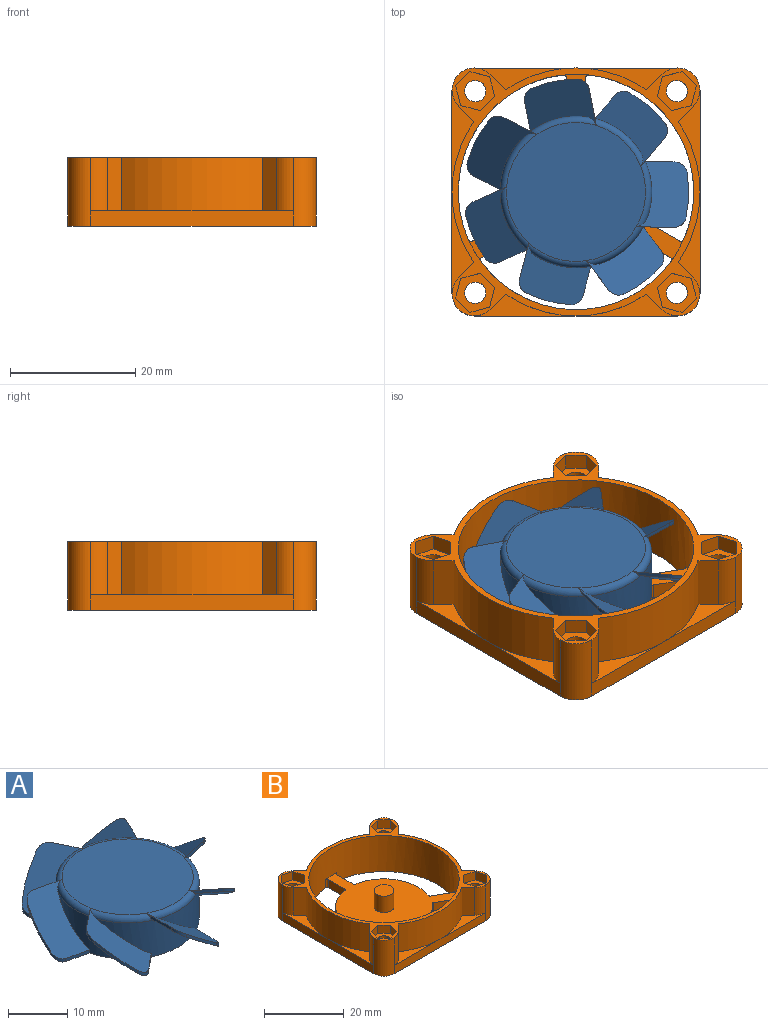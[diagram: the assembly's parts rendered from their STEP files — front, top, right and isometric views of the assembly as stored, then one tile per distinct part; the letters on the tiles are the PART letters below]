
ASSEMBLY  parts=2 mates=1
PART A: 67 faces, bbox 36.1x35.6x8.6 mm
  f0: torus R=11.1mm, axis (0,0,1), area 15.8mm2, adj f22,f25,f27,f37,f41
  f1: torus R=11.1mm, axis (0,0,1), area 15.8mm2, adj f18,f21,f23,f37,f40
  f2: torus R=11.1mm, axis (0,0,1), area 15.8mm2, adj f14,f17,f19,f37,f39
  f3: torus R=11.1mm, axis (0,0,1), area 15.8mm2, adj f10,f13,f15,f37,f38
  f4: torus R=11.1mm, axis (0,0,1), area 15.8mm2, adj f6,f9,f11,f34,f37
  f5: torus R=11.1mm, axis (0,0,1), area 15.8mm2, adj f7,f30,f33,f35,f37
  f6: plane 11.46x8.73mm, normal (0.13,0.58,-0.8), area 78mm2, adj f4,f8,f9,f34,f49,f52,f53
  f7: plane 11.36x9.65mm, normal (-0.13,-0.58,0.8), area 78.4mm2, adj f5,f8,f9,f35,f49,f52,f53
  f8: plane 4.65x1.06mm, normal (-0.22,-0.97,0), area 3mm2, adj f6,f7,f35,f52
  f9: plane 5.85x1.42mm, normal (0.22,0.97,0), area 3.2mm2, adj f4,f6,f7,f53
  f10: plane 5.41x2.67mm, normal (0.9,0.43,0), area 3.2mm2, adj f3,f11,f13,f54
  f11: plane 12.23x10mm, normal (-0.54,-0.26,0.8), area 78.4mm2, adj f4,f10,f12,f34,f48,f54,f55
  f12: plane 4.29x2.07mm, normal (-0.9,-0.43,0), area 3mm2, adj f11,f13,f34,f55
  f13: plane 11.88x10.1mm, normal (0.54,0.26,-0.8), area 78mm2, adj f3,f10,f12,f38,f48,f54,f55
  f14: plane 5.41x2.67mm, normal (0.9,-0.43,0), area 3.2mm2, adj f2,f15,f17,f56
  f15: plane 11.74x11.01mm, normal (-0.54,0.26,0.8), area 78.4mm2, adj f3,f14,f16,f38,f47,f56,f57
  f16: plane 4.29x2.07mm, normal (-0.9,0.43,0), area 3mm2, adj f15,f17,f38,f57
  f17: plane 11.84x10.17mm, normal (0.54,-0.26,-0.8), area 78mm2, adj f2,f14,f16,f39,f47,f56,f57
  f18: plane 5.85x1.42mm, normal (0.22,-0.97,0), area 3.2mm2, adj f1,f19,f21,f58
  f19: plane 11.61x8.55mm, normal (-0.13,0.58,0.8), area 78.4mm2, adj f2,f18,f20,f39,f46,f58,f59
  f20: plane 4.65x1.06mm, normal (-0.22,0.97,0), area 3mm2, adj f19,f21,f39,f59
  f21: plane 11.48x8.65mm, normal (0.13,-0.58,-0.8), area 78mm2, adj f1,f18,f20,f40,f46,f58,f59
  f22: plane 4.71x3.78mm, normal (-0.62,-0.78,0), area 3.2mm2, adj f0,f23,f25,f60
  f23: plane 11.92x11.63mm, normal (0.37,0.47,0.8), area 78.4mm2, adj f1,f22,f24,f40,f45,f60,f61
  f24: plane 3.73x2.97mm, normal (0.62,0.78,0), area 3mm2, adj f23,f25,f40,f61
  f25: plane 11.73x11.2mm, normal (-0.37,-0.47,-0.8), area 78mm2, adj f0,f22,f24,f41,f45,f60,f61
  f26: plane 6x0.74mm, normal (-1,0,0), area 3.2mm2, adj f27,f29,f62,f66
  f27: plane 10.51x8.23mm, normal (0.6,0,0.8), area 78.4mm2, adj f0,f26,f28,f41,f44,f62,f63
  f28: plane 4.76x0.63mm, normal (1,0,0), area 3mm2, adj f27,f29,f41,f63
  f29: plane 10.61x7.99mm, normal (-0.6,0,-0.8), area 78mm2, adj f26,f28,f42,f44,f62,f63,f66
  f30: plane 4.71x3.78mm, normal (-0.62,0.78,0), area 3.2mm2, adj f5,f31,f33,f64
  f31: plane 12.33x11.04mm, normal (0.37,-0.47,0.8), area 78.4mm2, adj f30,f32,f42,f43,f64,f65,f66
  f32: plane 3.73x2.97mm, normal (0.62,-0.78,0), area 3mm2, adj f31,f33,f42,f65
  f33: plane 11.78x11.14mm, normal (-0.37,0.47,-0.8), area 78mm2, adj f5,f30,f32,f35,f43,f64,f65
  f34: cylinder r=12.1mm len=14.71mm, axis (0,0,-1), area 75.4mm2, adj f4,f6,f11,f12,f36
  f35: cylinder r=12.1mm len=17.27mm, axis (0,0,-1), area 75.4mm2, adj f5,f7,f8,f33,f36
  f36: plane 24.2x24.2mm, normal (0,0,-1), area 440.3mm2, adj f34,f35,f38,f39,f40,f41,f42,f50
  f37: plane 22.2x22.2mm, normal (0,0,1), area 387.1mm2, adj f0,f1,f2,f3,f4,f5,f66
  f38: cylinder r=12.1mm len=17.96mm, axis (0,0,-1), area 75.4mm2, adj f3,f13,f15,f16,f36
  f39: cylinder r=12.1mm len=13.37mm, axis (0,0,-1), area 75.4mm2, adj f2,f17,f19,f20,f36
  f40: cylinder r=12.1mm len=17.74mm, axis (0,0,-1), area 75.4mm2, adj f1,f21,f23,f24,f36
  f41: cylinder r=12.1mm len=15.71mm, axis (0,0,-1), area 75.4mm2, adj f0,f25,f27,f28,f36
  f42: cylinder r=12.1mm len=16.64mm, axis (0,0,-1), area 75.4mm2, adj f29,f31,f32,f36,f66
  f43: cylinder r=18mm len=6.11mm, axis (0,0,1), area 4.6mm2, adj f31,f33,f64,f65
  f44: cylinder r=18mm len=7.31mm, axis (0,0,1), area 4.6mm2, adj f27,f29,f62,f63
  f45: cylinder r=18mm len=6.11mm, axis (0,0,1), area 4.6mm2, adj f23,f25,f60,f61
  f46: cylinder r=18mm len=7.13mm, axis (0,0,1), area 4.6mm2, adj f19,f21,f58,f59
  f47: cylinder r=18mm len=6.59mm, axis (0,0,1), area 4.6mm2, adj f15,f17,f56,f57
  f48: cylinder r=18mm len=6.59mm, axis (0,0,1), area 4.6mm2, adj f11,f13,f54,f55
  f49: cylinder r=18mm len=7.13mm, axis (0,0,1), area 4.6mm2, adj f6,f7,f52,f53
  f50: cylinder r=2.5mm len=5mm, axis (0,0,-1), area 78.5mm2, adj f36,f51
  f51: plane 5x5mm, normal (0,0,-1), area 19.6mm2, adj f50
  f52: cylinder r=2mm len=1.99mm, axis (0,0,1), area 1.7mm2, adj f6,f7,f8,f49
  f53: cylinder r=2mm len=2.26mm, axis (0,0,1), area 1.7mm2, adj f6,f7,f9,f49
  f54: cylinder r=2mm len=2.29mm, axis (0,0,1), area 1.7mm2, adj f10,f11,f13,f48
  f55: cylinder r=2mm len=2.46mm, axis (0,0,1), area 1.7mm2, adj f11,f12,f13,f48
  f56: cylinder r=2mm len=2.46mm, axis (0,0,1), area 1.7mm2, adj f14,f15,f17,f47
  f57: cylinder r=2mm len=2.29mm, axis (0,0,1), area 1.7mm2, adj f15,f16,f17,f47
  f58: cylinder r=2mm len=1.99mm, axis (0,0,1), area 1.7mm2, adj f18,f19,f21,f46
  f59: cylinder r=2mm len=2.26mm, axis (0,0,1), area 1.7mm2, adj f19,f20,f21,f46
  f60: cylinder r=2mm len=2.52mm, axis (0,0,1), area 1.7mm2, adj f22,f23,f25,f45
  f61: cylinder r=2mm len=2.47mm, axis (0,0,1), area 1.7mm2, adj f23,f24,f25,f45
  f62: cylinder r=2mm len=1.96mm, axis (0,0,1), area 1.7mm2, adj f26,f27,f29,f44
  f63: cylinder r=2mm len=1.96mm, axis (0,0,1), area 1.7mm2, adj f27,f28,f29,f44
  f64: cylinder r=2mm len=2.47mm, axis (0,0,1), area 1.7mm2, adj f30,f31,f33,f43
  f65: cylinder r=2mm len=2.52mm, axis (0,0,1), area 1.7mm2, adj f31,f32,f33,f43
  f66: torus R=11.1mm, axis (0,0,1), area 15.8mm2, adj f26,f29,f31,f37,f42
PART B: 99 faces, bbox 39.6x39.6x11 mm
  f0: cylinder r=1.7mm len=7.5mm, axis (0,0,1), area 80.1mm2, adj f74,f96
  f1: cylinder r=1.7mm len=7.5mm, axis (0,0,1), area 80.1mm2, adj f67,f94
  f2: cylinder r=1.7mm len=7.5mm, axis (0,0,1), area 80.1mm2, adj f60,f93
  f3: cylinder r=1.7mm len=7.5mm, axis (0,0,1), area 80.1mm2, adj f53,f95
  f4: plane 34.42x30.9mm, normal (0,0,1), area 501.4mm2, adj f12,f13,f14,f15,f16,f17,f21,f22
  f5: plane 16.2x3.49mm, normal (0,0,1), area 19mm2, adj f24,f28,f39,f45
  f6: plane 16.2x3.49mm, normal (0,0,1), area 19mm2, adj f24,f38,f39,f52
  f7: plane 16.2x3.49mm, normal (0,0,1), area 19mm2, adj f20,f36,f37,f51
  f8: plane 16.2x3.49mm, normal (0,0,1), area 19mm2, adj f20,f35,f36,f50
  f9: plane 16.2x3.49mm, normal (0,0,1), area 19mm2, adj f19,f33,f34,f49
  f10: plane 16.2x3.49mm, normal (0,0,1), area 19mm2, adj f19,f32,f33,f48
  f11: plane 16.2x3.49mm, normal (0,0,1), area 19mm2, adj f18,f30,f31,f47
  f12: cylinder r=12.1mm len=18.77mm, axis (0,0,-1), area 53.7mm2, adj f4,f27,f89,f92
  f13: plane 4.98x2.88mm, normal (-0.5,-0.87,0), area 14.4mm2, adj f4,f27,f89,f90
  f14: cylinder r=18.8mm len=37.6mm, axis (0,0,-1), area 1268.5mm2, adj f4,f27,f40,f83,f84,f87,f88,f90
  f15: plane 5.75x2.5mm, normal (-1,0,0), area 14.4mm2, adj f4,f27,f85,f88
  f16: cylinder r=12.1mm len=16.26mm, axis (0,0,-1), area 53.7mm2, adj f4,f27,f85,f86
  f17: plane 4.98x2.88mm, normal (-0.5,0.87,0), area 14.4mm2, adj f4,f27,f86,f87
  f18: plane 32.4x2.5mm, normal (0,1,0), area 81mm2, adj f11,f26,f27,f41,f44
  f19: plane 32.4x2.5mm, normal (-1,0,0), area 81mm2, adj f9,f10,f27,f41,f42
  f20: plane 32.4x2.5mm, normal (0,-1,0), area 81mm2, adj f7,f8,f27,f42,f43
  f21: plane 4.98x2.88mm, normal (0.5,0.87,0), area 14.4mm2, adj f4,f27,f81,f84
  f22: cylinder r=12.1mm len=16.26mm, axis (0,0,-1), area 53.7mm2, adj f4,f27,f81,f82
  f23: plane 5.75x2.5mm, normal (1,0,0), area 14.4mm2, adj f4,f27,f82,f83
  f24: plane 32.4x2.5mm, normal (1,0,0), area 81mm2, adj f5,f6,f27,f43,f44
  f25: plane 4.98x2.88mm, normal (0.5,-0.87,0), area 14.4mm2, adj f4,f27,f91,f92
  f26: plane 16.2x3.49mm, normal (0,0,1), area 19mm2, adj f18,f29,f30,f46
  f27: plane 39.6x39.6mm, normal (0,0,-1), area 876.1mm2, adj f12,f13,f14,f15,f16,f17,f18,f19
  f28: plane 8.5x2.32mm, normal (0.71,-0.71,0), area 27.9mm2, adj f5,f39,f40,f45
  f29: plane 8.5x2.32mm, normal (-0.71,0.71,0), area 27.9mm2, adj f26,f30,f40,f46
  f30: cylinder r=19.8mm len=22.44mm, axis (0,0,-1), area 202.8mm2, adj f11,f26,f29,f31,f40
  f31: plane 8.5x2.32mm, normal (0.71,0.71,0), area 27.9mm2, adj f11,f30,f40,f47
  f32: plane 8.5x2.32mm, normal (-0.71,-0.71,0), area 27.9mm2, adj f10,f33,f40,f48
  f33: cylinder r=19.8mm len=22.44mm, axis (0,0,-1), area 202.8mm2, adj f9,f10,f32,f34,f40
  f34: plane 8.5x2.32mm, normal (-0.71,0.71,0), area 27.9mm2, adj f9,f33,f40,f49
  f35: plane 8.5x2.32mm, normal (0.71,-0.71,0), area 27.9mm2, adj f8,f36,f40,f50
  f36: cylinder r=19.8mm len=22.44mm, axis (0,0,-1), area 202.8mm2, adj f7,f8,f35,f37,f40
  f37: plane 8.5x2.32mm, normal (-0.71,-0.71,0), area 27.9mm2, adj f7,f36,f40,f51
  f38: plane 8.5x2.32mm, normal (0.71,0.71,0), area 27.9mm2, adj f6,f39,f40,f52
  f39: cylinder r=19.8mm len=22.44mm, axis (0,0,-1), area 202.8mm2, adj f5,f6,f28,f38,f40
  f40: plane 39.6x39.6mm, normal (0,0,1), area 185.8mm2, adj f14,f28,f29,f30,f31,f32,f33,f34
  f41: cylinder r=3.6mm len=11mm, axis (0,0,-1), area 62.2mm2, adj f18,f19,f27,f40,f47,f48
  f42: cylinder r=3.6mm len=11mm, axis (0,0,1), area 62.2mm2, adj f19,f20,f27,f40,f49,f50
  f43: cylinder r=3.6mm len=11mm, axis (0,0,-1), area 62.2mm2, adj f20,f24,f27,f40,f51,f52
  f44: cylinder r=3.6mm len=11mm, axis (0,0,1), area 62.2mm2, adj f18,f24,f27,f40,f45,f46
  f45: cylinder r=4mm len=8.5mm, axis (0,0,-1), area 25.3mm2, adj f5,f28,f40,f44
  f46: cylinder r=4mm len=8.5mm, axis (0,0,-1), area 25.3mm2, adj f26,f29,f40,f44
  f47: cylinder r=4mm len=8.5mm, axis (0,0,-1), area 25.3mm2, adj f11,f31,f40,f41
  f48: cylinder r=4mm len=8.5mm, axis (0,0,-1), area 25.3mm2, adj f10,f32,f40,f41
  f49: cylinder r=4mm len=8.5mm, axis (0,0,-1), area 25.3mm2, adj f9,f34,f40,f42
  f50: cylinder r=4mm len=8.5mm, axis (0,0,-1), area 25.3mm2, adj f8,f35,f40,f42
  f51: cylinder r=4mm len=8.5mm, axis (0,0,-1), area 25.3mm2, adj f7,f37,f40,f43
  f52: cylinder r=4mm len=8.5mm, axis (0,0,-1), area 25.3mm2, adj f6,f38,f40,f43
  f53: plane 6.26x6.26mm, normal (0,0,1), area 18.2mm2, adj f3,f54,f55,f56,f57,f58,f59
  f54: plane 3.13x2.5mm, normal (-0.97,0.26,0), area 8.1mm2, adj f40,f53,f55,f59
  f55: plane 2.5x2.29mm, normal (-0.71,-0.71,0), area 8.1mm2, adj f40,f53,f54,f56
  f56: plane 3.13x2.5mm, normal (0.26,-0.97,0), area 8.1mm2, adj f40,f53,f55,f57
  f57: plane 3.13x2.5mm, normal (0.97,-0.26,0), area 8.1mm2, adj f40,f53,f56,f58
  f58: plane 2.5x2.29mm, normal (0.71,0.71,0), area 8.1mm2, adj f40,f53,f57,f59
  f59: plane 3.13x2.5mm, normal (-0.26,0.97,0), area 8.1mm2, adj f40,f53,f54,f58
  f60: plane 6.26x6.26mm, normal (0,0,1), area 18.2mm2, adj f2,f61,f62,f63,f64,f65,f66
  f61: plane 2.5x2.29mm, normal (-0.71,-0.71,0), area 8.1mm2, adj f40,f60,f62,f66
  f62: plane 3.13x2.5mm, normal (0.26,-0.97,0), area 8.1mm2, adj f40,f60,f61,f63
  f63: plane 3.13x2.5mm, normal (0.97,-0.26,0), area 8.1mm2, adj f40,f60,f62,f64
  f64: plane 2.5x2.29mm, normal (0.71,0.71,0), area 8.1mm2, adj f40,f60,f63,f65
  f65: plane 3.13x2.5mm, normal (-0.26,0.97,0), area 8.1mm2, adj f40,f60,f64,f66
  f66: plane 3.13x2.5mm, normal (-0.97,0.26,0), area 8.1mm2, adj f40,f60,f61,f65
  f67: plane 6.26x6.26mm, normal (0,0,1), area 18.2mm2, adj f1,f68,f69,f70,f71,f72,f73
  f68: plane 3.13x2.5mm, normal (-0.97,-0.26,0), area 8.1mm2, adj f40,f67,f69,f73
  f69: plane 3.13x2.5mm, normal (-0.26,-0.97,0), area 8.1mm2, adj f40,f67,f68,f70
  f70: plane 2.5x2.29mm, normal (0.71,-0.71,0), area 8.1mm2, adj f40,f67,f69,f71
  f71: plane 3.13x2.5mm, normal (0.97,0.26,0), area 8.1mm2, adj f40,f67,f70,f72
  f72: plane 3.13x2.5mm, normal (0.26,0.97,0), area 8.1mm2, adj f40,f67,f71,f73
  f73: plane 2.5x2.29mm, normal (-0.71,0.71,0), area 8.1mm2, adj f40,f67,f68,f72
  f74: plane 6.26x6.26mm, normal (0,0,1), area 18.2mm2, adj f0,f75,f76,f77,f78,f79,f80
  f75: plane 3.13x2.5mm, normal (-0.97,-0.26,0), area 8.1mm2, adj f40,f74,f76,f80
  f76: plane 3.13x2.5mm, normal (-0.26,-0.97,0), area 8.1mm2, adj f40,f74,f75,f77
  f77: plane 2.5x2.29mm, normal (0.71,-0.71,0), area 8.1mm2, adj f40,f74,f76,f78
  f78: plane 3.13x2.5mm, normal (0.97,0.26,0), area 8.1mm2, adj f40,f74,f77,f79
  f79: plane 3.13x2.5mm, normal (0.26,0.97,0), area 8.1mm2, adj f40,f74,f78,f80
  f80: plane 2.5x2.29mm, normal (-0.71,0.71,0), area 8.1mm2, adj f40,f74,f75,f79
  f81: cylinder r=0.5mm len=2.5mm, axis (0,0,-1), area 1.8mm2, adj f4,f21,f22,f27
  f82: cylinder r=0.5mm len=2.5mm, axis (0,0,-1), area 1.8mm2, adj f4,f22,f23,f27
  f83: cylinder r=0.5mm len=2.5mm, axis (0,0,-1), area 2.1mm2, adj f4,f14,f23,f27
  f84: cylinder r=0.5mm len=2.5mm, axis (0,0,-1), area 2.1mm2, adj f4,f14,f21,f27
  f85: cylinder r=0.5mm len=2.5mm, axis (0,0,-1), area 1.8mm2, adj f4,f15,f16,f27
  f86: cylinder r=0.5mm len=2.5mm, axis (0,0,-1), area 1.8mm2, adj f4,f16,f17,f27
  f87: cylinder r=0.5mm len=2.5mm, axis (0,0,-1), area 2.1mm2, adj f4,f14,f17,f27
  f88: cylinder r=0.5mm len=2.5mm, axis (0,0,-1), area 2.1mm2, adj f4,f14,f15,f27
  f89: cylinder r=0.5mm len=2.5mm, axis (0,0,-1), area 1.8mm2, adj f4,f12,f13,f27
  f90: cylinder r=0.5mm len=2.5mm, axis (0,0,-1), area 2.1mm2, adj f4,f13,f14,f27
  f91: cylinder r=0.5mm len=2.5mm, axis (0,0,-1), area 2.1mm2, adj f4,f14,f25,f27
  f92: cylinder r=0.5mm len=2.5mm, axis (0,0,-1), area 1.8mm2, adj f4,f12,f25,f27
  f93: cone r=1.7mm half-angle=45deg, axis (0,0,-1), area 19.5mm2, adj f2,f27
  f94: cone r=1.7mm half-angle=45deg, axis (0,0,-1), area 19.5mm2, adj f1,f27
  f95: cone r=1.7mm half-angle=45deg, axis (0,0,-1), area 19.5mm2, adj f3,f27
  f96: cone r=1.7mm half-angle=45deg, axis (0,0,-1), area 19.5mm2, adj f0,f27
  f97: cylinder r=2.5mm len=5mm, axis (0,0,-1), area 78.5mm2, adj f4,f98
  f98: plane 5x5mm, normal (0,0,1), area 19.6mm2, adj f97
PLACE A rot(axis=(0,0,1),36.9deg) t=(3.46,16.64,5.78)mm
PLACE B t=(-16.34,-3.16,3.28)mm fixed
MATE revolute A.f0 <-> B.f12  axis (0,0,-1) through (3.46,16.64,10.78)mm
